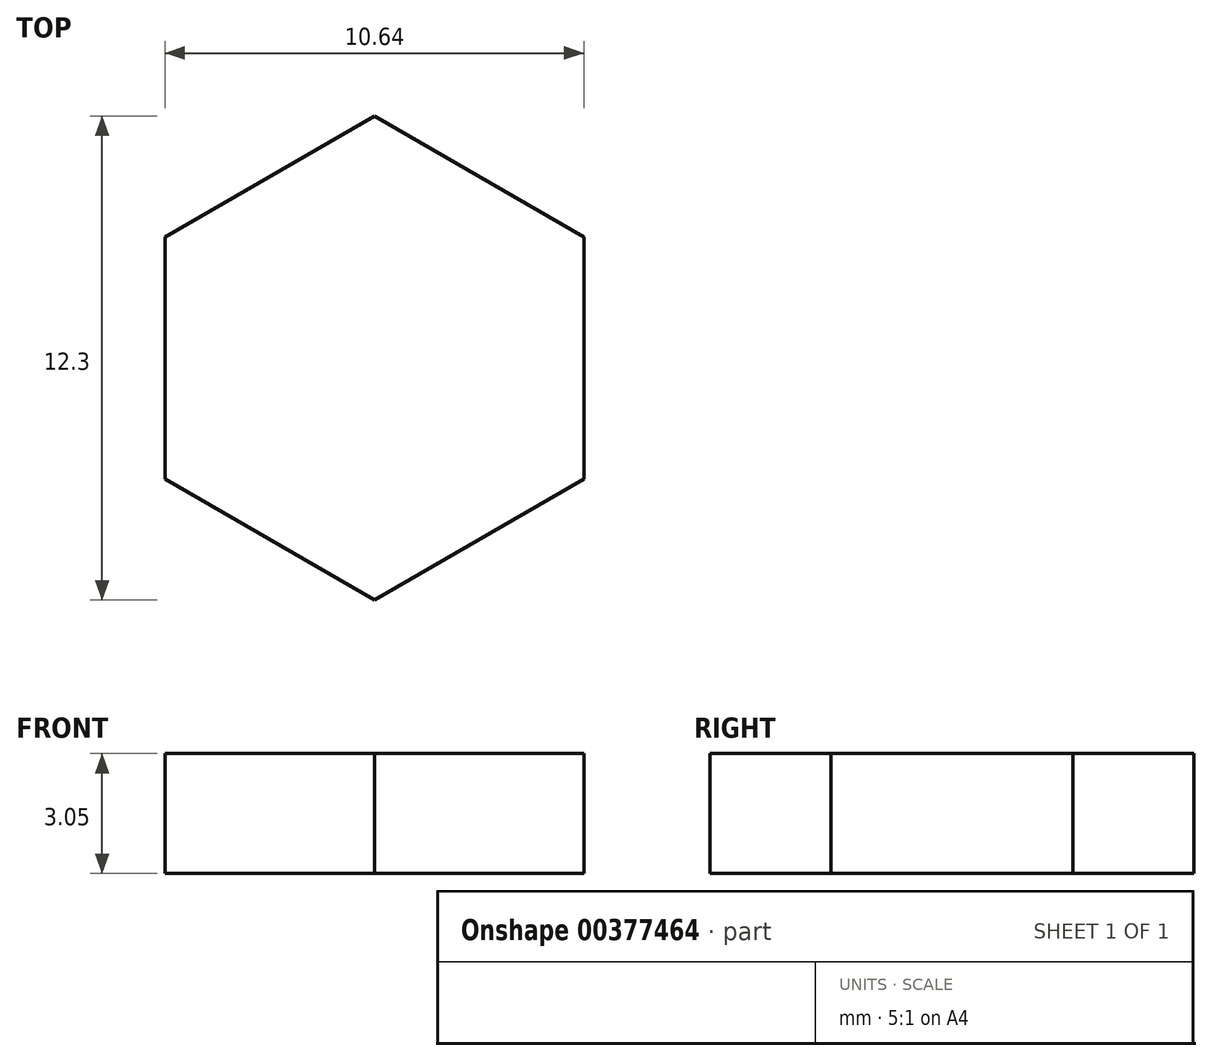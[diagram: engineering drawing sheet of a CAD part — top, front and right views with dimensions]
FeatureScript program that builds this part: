
annotation { "Feature Type Name" : "Feature", "Feature Type Description" : "" }
export const myFeature = defineFeature(function(context is Context, id is Id, definition is map)
    precondition{}
    {
        {
            var Q0;
            Q0=qCreatedBy(makeId("Top.planeOp"),FACE);
            var sketch = newSketch(context, id + "F0", { "sketchPlane" : qUnion([Q0])});
            skCircle(sketch, "E0.cCircle", {"center": v(0, 0) * mm, "radius": 5.32 * mm, "construction": true});
            skLineSegment(sketch, "E0.0", {"start": v(5.32, 3.07) * mm, "end": v(5.32, -3.07) * mm});
            skLineSegment(sketch, "E0.1", {"start": v(5.32, -3.07) * mm, "end": v(0, -6.15) * mm});
            skLineSegment(sketch, "E0.2", {"start": v(0, -6.15) * mm, "end": v(-5.32, -3.07) * mm});
            skLineSegment(sketch, "E0.3", {"start": v(-5.32, -3.07) * mm, "end": v(-5.32, 3.07) * mm});
            skLineSegment(sketch, "E0.4", {"start": v(-5.32, 3.07) * mm, "end": v(0, 6.15) * mm});
            skLineSegment(sketch, "E0.5", {"start": v(0, 6.15) * mm, "end": v(5.32, 3.07) * mm});
            skPoint(sketch, "E0.0.midPoint", {"position": v(5.32, 0) * mm});
            skSolve(sketch);
        }
        {
            var Q0;
            Q0=makeQuery(id+"F0.imprint","IMPRINT",FACE,{"disambiguationData":[TD([[makeQuery(id+"F0.imprint","IMPRINT",EDGE,{"derivedFrom":sQuery(id+"F0.wireOp",EDGE,"E0.0")}),-1.0]])]});
            extrude(context, id + "F1", {"entities" : qUnion([Q0]), "depth" : 3.05 * mm});
        }
    });
